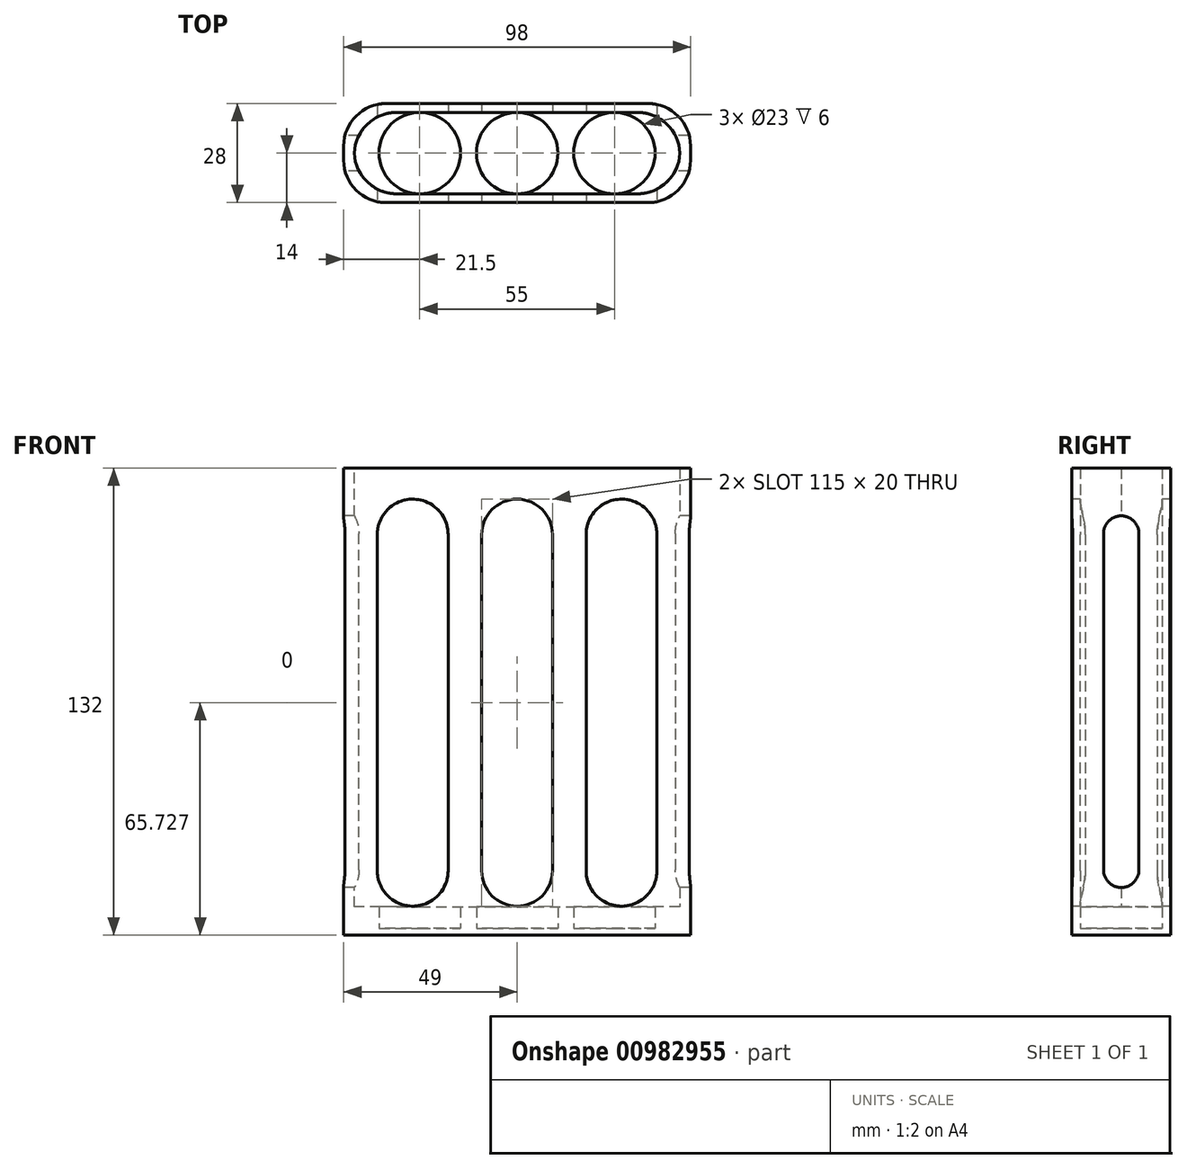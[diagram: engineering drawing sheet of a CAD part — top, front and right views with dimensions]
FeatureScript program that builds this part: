
annotation { "Feature Type Name" : "Feature", "Feature Type Description" : "" }
export const myFeature = defineFeature(function(context is Context, id is Id, definition is map)
    precondition{}
    {
        {
            var Q0;
            Q0=qCreatedBy(makeId("Top.planeOp"),FACE);
            var sketch = newSketch(context, id + "F0", { "sketchPlane" : qUnion([Q0])});
            skCircle(sketch, "E0", {"center": v(-34.5, 0) * mm, "radius": 11.5 * mm});
            skCircle(sketch, "E1.1.0.0", {"center": v(-11.5, 0) * mm, "radius": 11.5 * mm});
            skCircle(sketch, "E1.2.0.0", {"center": v(11.5, 0) * mm, "radius": 11.5 * mm});
            skCircle(sketch, "E1.3.0.0", {"center": v(34.5, 0) * mm, "radius": 11.5 * mm});
            skLineSegment(sketch, "E1.direction1", {"start": v(-34.5, 0) * mm, "end": v(-11.5, 0) * mm, "construction": true});
            skPoint(sketch, "E2", {"position": v(0, 0) * mm});
            skLineSegment(sketch, "E3.bottom", {"start": v(-34.5, 11.5) * mm, "end": v(34.5, 11.5) * mm});
            skLineSegment(sketch, "E3.top", {"start": v(-34.5, -11.5) * mm, "end": v(34.5, -11.5) * mm});
            skLineSegment(sketch, "E3.left", {"start": v(-34.5, 11.5) * mm, "end": v(-34.5, -11.5) * mm});
            skLineSegment(sketch, "E3.right", {"start": v(34.5, 11.5) * mm, "end": v(34.5, -11.5) * mm});
            skLineSegment(sketch, "E4.bottom", {"start": v(49, 14) * mm, "end": v(-49, 14) * mm});
            skLineSegment(sketch, "E4.top", {"start": v(49, -14) * mm, "end": v(-49, -14) * mm});
            skLineSegment(sketch, "E4.left", {"start": v(49, 14) * mm, "end": v(49, -14) * mm});
            skLineSegment(sketch, "E4.right", {"start": v(-49, 14) * mm, "end": v(-49, -14) * mm});
            skLineSegment(sketch, "E5.bottom", {"start": v(-34.5, 11.5) * mm, "end": v(-46, 11.5) * mm});
            skLineSegment(sketch, "E5.top", {"start": v(-34.5, 0) * mm, "end": v(-46, 0) * mm});
            skLineSegment(sketch, "E5.left", {"start": v(-34.5, 11.5) * mm, "end": v(-34.5, 0) * mm});
            skLineSegment(sketch, "E5.right", {"start": v(-46, 11.5) * mm, "end": v(-46, 0) * mm});
            skLineSegment(sketch, "E6.bottom", {"start": v(-46, 0) * mm, "end": v(-34.5, 0) * mm});
            skLineSegment(sketch, "E6.top", {"start": v(-46, -11.5) * mm, "end": v(-34.5, -11.5) * mm});
            skLineSegment(sketch, "E6.left", {"start": v(-46, 0) * mm, "end": v(-46, -11.5) * mm});
            skLineSegment(sketch, "E6.right", {"start": v(-34.5, 0) * mm, "end": v(-34.5, -11.5) * mm});
            skLineSegment(sketch, "E7.bottom", {"start": v(34.5, 11.5) * mm, "end": v(46, 11.5) * mm});
            skLineSegment(sketch, "E7.top", {"start": v(34.5, 0) * mm, "end": v(46, 0) * mm});
            skLineSegment(sketch, "E7.left", {"start": v(34.5, 11.5) * mm, "end": v(34.5, 0) * mm});
            skLineSegment(sketch, "E7.right", {"start": v(46, 11.5) * mm, "end": v(46, 0) * mm});
            skLineSegment(sketch, "E8.top", {"start": v(34.5, -11.5) * mm, "end": v(46, -11.5) * mm});
            skLineSegment(sketch, "E8.left", {"start": v(34.5, 0) * mm, "end": v(34.5, -11.5) * mm});
            skLineSegment(sketch, "E8.right", {"start": v(46, 0) * mm, "end": v(46, -11.5) * mm});
            skSolve(sketch);
        }
        {
            var Q0;
            Q0=makeQuery(id+"F0.imprint","IMPRINT",FACE,{"disambiguationData":[TD([[makeQuery(id+"F0.imprint","IMPRINT",EDGE,{"derivedFrom":sQuery(id+"F0.wireOp",EDGE,"E4.bottom")}),1.0]])]});
            var Q1;
            {var subQ0=sQuery(id+"F0.wireOp",EDGE,"E3.left");Q1=makeQuery(id+"F0.imprint","IMPRINT",FACE,{"disambiguationData":[TD([[makeQuery(id+"F0.imprint","IMPRINT",EDGE,{"derivedFrom":subQ0}),-1.0]])]});}
            var Q2;
            {var subQ0=sQuery(id+"F0.wireOp",EDGE,"E3.left");Q2=makeQuery(id+"F0.imprint","IMPRINT",FACE,{"disambiguationData":[TD([[makeQuery(id+"F0.imprint","IMPRINT",EDGE,{"derivedFrom":subQ0}),1.0]])]});}
            var Q3;
            {var subQ1=sQuery(id+"F0.wireOp",EDGE,"E0");var subQ3=sQuery(id+"F0.wireOp",EDGE,"E1.1.0.0");var subQ4=makeQuery(id+"F0.imprint","INTERSECT",VERTEX,{"derivedFrom":[subQ1,subQ3]});Q3=makeQuery(id+"F0.imprint","IMPRINT",FACE,{"disambiguationData":[TD([[makeQuery(id+"F0.imprint","IMPRINT",EDGE,{"disambiguationData":[TD([[subQ4,-1.0]])],"derivedFrom":subQ3}),-1.0]])]});}
            var Q4;
            {var subQ0=sQuery(id+"F0.wireOp",EDGE,"E1.1.0.0");var subQ1=makeQuery(id+"F0.imprint","INTERSECT",VERTEX,{"derivedFrom":[subQ0,sQuery(id+"F0.wireOp",EDGE,"E3.bottom")]});Q4=makeQuery(id+"F0.imprint","IMPRINT",FACE,{"disambiguationData":[TD([[makeQuery(id+"F0.imprint","IMPRINT",EDGE,{"disambiguationData":[TD([[subQ1,1.0]])],"derivedFrom":subQ0}),1.0]])]});}
            var Q5;
            {var subQ1=sQuery(id+"F0.wireOp",EDGE,"E0");var subQ3=sQuery(id+"F0.wireOp",EDGE,"E1.1.0.0");var subQ4=makeQuery(id+"F0.imprint","INTERSECT",VERTEX,{"derivedFrom":[subQ1,subQ3]});Q5=makeQuery(id+"F0.imprint","IMPRINT",FACE,{"disambiguationData":[TD([[makeQuery(id+"F0.imprint","IMPRINT",EDGE,{"disambiguationData":[TD([[subQ4,1.0]])],"derivedFrom":subQ3}),-1.0]])]});}
            var Q6;
            {var subQ0=sQuery(id+"F0.wireOp",EDGE,"E1.2.0.0");var subQ1=sQuery(id+"F0.wireOp",EDGE,"E1.1.0.0");var subQ2=makeQuery(id+"F0.imprint","INTERSECT",VERTEX,{"derivedFrom":[subQ1,subQ0]});Q6=makeQuery(id+"F0.imprint","IMPRINT",FACE,{"disambiguationData":[TD([[makeQuery(id+"F0.imprint","IMPRINT",EDGE,{"disambiguationData":[TD([[subQ2,1.0]])],"derivedFrom":subQ1}),-1.0]])]});}
            var Q7;
            {var subQ0=sQuery(id+"F0.wireOp",EDGE,"E3.bottom");var subQ1=sQuery(id+"F0.wireOp",EDGE,"E1.1.0.0");var subQ2=makeQuery(id+"F0.imprint","INTERSECT",VERTEX,{"derivedFrom":[subQ1,subQ0]});Q7=makeQuery(id+"F0.imprint","IMPRINT",FACE,{"disambiguationData":[TD([[makeQuery(id+"F0.imprint","IMPRINT",EDGE,{"disambiguationData":[TD([[subQ2,1.0]])],"derivedFrom":subQ1}),-1.0]])]});}
            var Q8;
            {var subQ0=sQuery(id+"F0.wireOp",EDGE,"E1.2.0.0");var subQ1=makeQuery(id+"F0.imprint","INTERSECT",VERTEX,{"derivedFrom":[subQ0,sQuery(id+"F0.wireOp",EDGE,"E3.bottom")]});Q8=makeQuery(id+"F0.imprint","IMPRINT",FACE,{"disambiguationData":[TD([[makeQuery(id+"F0.imprint","IMPRINT",EDGE,{"disambiguationData":[TD([[subQ1,1.0]])],"derivedFrom":subQ0}),1.0]])]});}
            var Q9;
            {var subQ0=sQuery(id+"F0.wireOp",EDGE,"E3.right");Q9=makeQuery(id+"F0.imprint","IMPRINT",FACE,{"disambiguationData":[TD([[makeQuery(id+"F0.imprint","IMPRINT",EDGE,{"derivedFrom":subQ0}),-1.0]])]});}
            var Q10;
            {var subQ0=sQuery(id+"F0.wireOp",EDGE,"E3.right");Q10=makeQuery(id+"F0.imprint","IMPRINT",FACE,{"disambiguationData":[TD([[makeQuery(id+"F0.imprint","IMPRINT",EDGE,{"derivedFrom":subQ0}),1.0]])]});}
            var Q11;
            {var subQ0=sQuery(id+"F0.wireOp",EDGE,"E1.3.0.0");var subQ1=sQuery(id+"F0.wireOp",EDGE,"E1.2.0.0");var subQ2=makeQuery(id+"F0.imprint","INTERSECT",VERTEX,{"derivedFrom":[subQ1,subQ0]});Q11=makeQuery(id+"F0.imprint","IMPRINT",FACE,{"disambiguationData":[TD([[makeQuery(id+"F0.imprint","IMPRINT",EDGE,{"disambiguationData":[TD([[subQ2,1.0]])],"derivedFrom":subQ1}),-1.0]])]});}
            var Q12;
            {var subQ0=sQuery(id+"F0.wireOp",EDGE,"E3.bottom");var subQ1=sQuery(id+"F0.wireOp",EDGE,"E1.2.0.0");var subQ2=makeQuery(id+"F0.imprint","INTERSECT",VERTEX,{"derivedFrom":[subQ1,subQ0]});Q12=makeQuery(id+"F0.imprint","IMPRINT",FACE,{"disambiguationData":[TD([[makeQuery(id+"F0.imprint","IMPRINT",EDGE,{"disambiguationData":[TD([[subQ2,1.0]])],"derivedFrom":subQ1}),-1.0]])]});}
            var Q13;
            {var subQ0=sQuery(id+"F0.wireOp",EDGE,"E5.left");Q13=makeQuery(id+"F0.imprint","IMPRINT",FACE,{"disambiguationData":[TD([[makeQuery(id+"F0.imprint","IMPRINT",EDGE,{"derivedFrom":subQ0}),-1.0]])]});}
            var Q14;
            {var subQ2=sQuery(id+"F0.wireOp",EDGE,"E6.bottom");Q14=makeQuery(id+"F0.imprint","IMPRINT",FACE,{"disambiguationData":[TD([[makeQuery(id+"F0.imprint","IMPRINT",EDGE,{"derivedFrom":subQ2}),-1.0]])]});}
            var Q15;
            {var subQ0=sQuery(id+"F0.wireOp",EDGE,"E6.top");Q15=makeQuery(id+"F0.imprint","IMPRINT",FACE,{"disambiguationData":[TD([[makeQuery(id+"F0.imprint","IMPRINT",EDGE,{"derivedFrom":subQ0}),1.0]])]});}
            var Q16;
            {var subQ0=sQuery(id+"F0.wireOp",EDGE,"E5.left");Q16=makeQuery(id+"F0.imprint","IMPRINT",FACE,{"disambiguationData":[TD([[makeQuery(id+"F0.imprint","IMPRINT",EDGE,{"derivedFrom":subQ0}),1.0]])]});}
            var Q17;
            {var subQ0=sQuery(id+"F0.wireOp",EDGE,"E5.bottom");Q17=makeQuery(id+"F0.imprint","IMPRINT",FACE,{"disambiguationData":[TD([[makeQuery(id+"F0.imprint","IMPRINT",EDGE,{"derivedFrom":subQ0}),1.0]])]});}
            var Q18;
            {var subQ0=sQuery(id+"F0.wireOp",EDGE,"E7.left");Q18=makeQuery(id+"F0.imprint","IMPRINT",FACE,{"disambiguationData":[TD([[makeQuery(id+"F0.imprint","IMPRINT",EDGE,{"derivedFrom":subQ0}),-1.0]])]});}
            var Q19;
            {var subQ0=sQuery(id+"F0.wireOp",EDGE,"E7.left");Q19=makeQuery(id+"F0.imprint","IMPRINT",FACE,{"disambiguationData":[TD([[makeQuery(id+"F0.imprint","IMPRINT",EDGE,{"derivedFrom":subQ0}),1.0]])]});}
            var Q20;
            {var subQ0=sQuery(id+"F0.wireOp",EDGE,"E7.bottom");Q20=makeQuery(id+"F0.imprint","IMPRINT",FACE,{"disambiguationData":[TD([[makeQuery(id+"F0.imprint","IMPRINT",EDGE,{"derivedFrom":subQ0}),-1.0]])]});}
            var Q21;
            {var subQ2=sQuery(id+"F0.wireOp",EDGE,"E7.top");Q21=makeQuery(id+"F0.imprint","IMPRINT",FACE,{"disambiguationData":[TD([[makeQuery(id+"F0.imprint","IMPRINT",EDGE,{"derivedFrom":subQ2}),-1.0]])]});}
            var Q22;
            {var subQ0=sQuery(id+"F0.wireOp",EDGE,"E8.top");Q22=makeQuery(id+"F0.imprint","IMPRINT",FACE,{"disambiguationData":[TD([[makeQuery(id+"F0.imprint","IMPRINT",EDGE,{"derivedFrom":subQ0}),1.0]])]});}
            extrude(context, id + "F1", {"entities" : qUnion([Q0, Q1, Q2, Q3, Q4, Q5, Q6, Q7, Q8, Q9, Q10, Q11, Q12, Q13, Q14, Q15, Q16, Q17, Q18, Q19, Q20, Q21, Q22]), "oppositeDirection" : true, "depth" : 2 * mm, "offsetDistance" : 25 * mm});
        }
        {
            var Q0;
            Q0=makeQuery(id+"F0.imprint","IMPRINT",FACE,{"disambiguationData":[TD([[makeQuery(id+"F0.imprint","IMPRINT",EDGE,{"derivedFrom":sQuery(id+"F0.wireOp",EDGE,"E4.bottom")}),1.0]])]});
            extrude(context, id + "F2", {"entities" : qUnion([Q0]), "operationType" : NewBodyOperationType.ADD, "depth" : 130 * mm, "offsetDistance" : 25 * mm});
        }
        {
            var Q0;
            {var subQ0=sQuery(id+"F0.wireOp",EDGE,"E4.right");var subQ1=sQuery(id+"F0.wireOp",EDGE,"E4.bottom");Q0=makeQuery(id+"F2.boolean.opBoolean","MERGE",EDGE,{"derivedFrom":[makeQuery(id+"F1.opExtrude","SWEPT_EDGE",EDGE,{"disambiguationData":[OSD([subQ1,subQ0])]}),makeQuery(id+"F2.opExtrude","SWEPT_EDGE",EDGE,{"disambiguationData":[OSD([subQ1,subQ0])]})]});}
            var Q1;
            {var subQ0=sQuery(id+"F0.wireOp",EDGE,"E4.right");var subQ1=sQuery(id+"F0.wireOp",EDGE,"E4.top");Q1=makeQuery(id+"F2.boolean.opBoolean","MERGE",EDGE,{"derivedFrom":[makeQuery(id+"F1.opExtrude","SWEPT_EDGE",EDGE,{"disambiguationData":[OSD([subQ1,subQ0])]}),makeQuery(id+"F2.opExtrude","SWEPT_EDGE",EDGE,{"disambiguationData":[OSD([subQ1,subQ0])]})]});}
            var Q2;
            {var subQ0=sQuery(id+"F0.wireOp",EDGE,"E4.left");var subQ1=sQuery(id+"F0.wireOp",EDGE,"E4.top");Q2=makeQuery(id+"F2.boolean.opBoolean","MERGE",EDGE,{"derivedFrom":[makeQuery(id+"F1.opExtrude","SWEPT_EDGE",EDGE,{"disambiguationData":[OSD([subQ1,subQ0])]}),makeQuery(id+"F2.opExtrude","SWEPT_EDGE",EDGE,{"disambiguationData":[OSD([subQ1,subQ0])]})]});}
            var Q3;
            {var subQ0=sQuery(id+"F0.wireOp",EDGE,"E4.left");var subQ1=sQuery(id+"F0.wireOp",EDGE,"E4.bottom");Q3=makeQuery(id+"F2.boolean.opBoolean","MERGE",EDGE,{"derivedFrom":[makeQuery(id+"F1.opExtrude","SWEPT_EDGE",EDGE,{"disambiguationData":[OSD([subQ1,subQ0])]}),makeQuery(id+"F2.opExtrude","SWEPT_EDGE",EDGE,{"disambiguationData":[OSD([subQ1,subQ0])]})]});}
            var Q4;
            Q4=makeQuery(id+"F2.opExtrude","SWEPT_EDGE",EDGE,{"disambiguationData":[OSD([sQuery(id+"F0.wireOp",EDGE,"E7.bottom"),sQuery(id+"F0.wireOp",EDGE,"E7.right")])]});
            var Q5;
            Q5=makeQuery(id+"F2.opExtrude","SWEPT_EDGE",EDGE,{"disambiguationData":[OSD([sQuery(id+"F0.wireOp",EDGE,"E8.top"),sQuery(id+"F0.wireOp",EDGE,"E8.right")])]});
            var Q6;
            Q6=makeQuery(id+"F2.opExtrude","SWEPT_EDGE",EDGE,{"disambiguationData":[OSD([sQuery(id+"F0.wireOp",EDGE,"E5.bottom"),sQuery(id+"F0.wireOp",EDGE,"E5.right")])]});
            var Q7;
            Q7=makeQuery(id+"F2.opExtrude","SWEPT_EDGE",EDGE,{"disambiguationData":[OSD([sQuery(id+"F0.wireOp",EDGE,"E6.top"),sQuery(id+"F0.wireOp",EDGE,"E6.left")])]});
            fillet(context, id + "F3", {"entities" : qUnion([Q0, Q1, Q2, Q3, Q4, Q5, Q6, Q7]), "radius" : 12 * mm, "tangentPropagation" : true, "allowEdgeOverflow" : false});
        }
        {
            var Q0;
            {var subQ0=sQuery(id+"F0.wireOp",EDGE,"E4.top");Q0=makeQuery(id+"F2.boolean.opBoolean","MERGE",FACE,{"derivedFrom":[makeQuery(id+"F1.opExtrude","SWEPT_FACE",FACE,{"disambiguationData":[OSD([subQ0])]}),makeQuery(id+"F2.opExtrude","SWEPT_FACE",FACE,{"disambiguationData":[OSD([subQ0])]})]});}
            var sketch = newSketch(context, id + "F4", { "sketchPlane" : qUnion([Q0])});
            skLineSegment(sketch, "E9.bottom", {"start": v(-10, 111.23) * mm, "end": v(10, 111.23) * mm});
            skLineSegment(sketch, "E9.top", {"start": v(-10, 16.23) * mm, "end": v(10, 16.23) * mm});
            skLineSegment(sketch, "E9.left", {"start": v(-10, 111.23) * mm, "end": v(-10, 16.23) * mm});
            skLineSegment(sketch, "E9.right", {"start": v(10, 111.23) * mm, "end": v(10, 16.23) * mm});
            skPoint(sketch, "E9.middle", {"position": v(0, 63.73) * mm});
            skArc(sketch, "E10", {"start": v(10, 111.23) * mm, "mid": v(0, 121.23) * mm, "end": v(-10, 111.23) * mm});
            skArc(sketch, "E11", {"start": v(-10, 16.23) * mm, "mid": v(0, 6.23) * mm, "end": v(10, 16.23) * mm});
            skLineSegment(sketch, "E12.bottom", {"start": v(-19.5, 111.23) * mm, "end": v(-39.5, 111.23) * mm});
            skLineSegment(sketch, "E12.top", {"start": v(-19.5, 16.23) * mm, "end": v(-39.5, 16.23) * mm});
            skLineSegment(sketch, "E12.left", {"start": v(-19.5, 111.23) * mm, "end": v(-19.5, 16.23) * mm});
            skLineSegment(sketch, "E12.right", {"start": v(-39.5, 111.23) * mm, "end": v(-39.5, 16.23) * mm});
            skPoint(sketch, "E12.middle", {"position": v(-29.5, 63.73) * mm});
            skArc(sketch, "E13", {"start": v(-19.5, 111.23) * mm, "mid": v(-29.5, 121.23) * mm, "end": v(-39.5, 111.23) * mm});
            skArc(sketch, "E14", {"start": v(-39.5, 16.23) * mm, "mid": v(-29.5, 6.23) * mm, "end": v(-19.5, 16.23) * mm});
            skLineSegment(sketch, "E15.bottom", {"start": v(39.5, 111.23) * mm, "end": v(19.5, 111.23) * mm});
            skLineSegment(sketch, "E15.top", {"start": v(39.5, 16.23) * mm, "end": v(19.5, 16.23) * mm});
            skLineSegment(sketch, "E15.left", {"start": v(39.5, 111.23) * mm, "end": v(39.5, 16.23) * mm});
            skLineSegment(sketch, "E15.right", {"start": v(19.5, 111.23) * mm, "end": v(19.5, 16.23) * mm});
            skPoint(sketch, "E15.middle", {"position": v(29.5, 63.73) * mm});
            skArc(sketch, "E16", {"start": v(39.5, 111.23) * mm, "mid": v(29.5, 121.23) * mm, "end": v(19.5, 111.23) * mm});
            skArc(sketch, "E17", {"start": v(19.5, 16.23) * mm, "mid": v(29.5, 6.23) * mm, "end": v(39.5, 16.23) * mm});
            skLineSegment(sketch, "E18", {"start": v(0, 130) * mm, "end": v(0, -2) * mm, "construction": true});
            skSolve(sketch);
        }
        {
            var Q0;
            {var subQ0=sQuery(id+"F4.wireOp",EDGE,"E12.left");Q0=makeQuery(id+"F4.imprint","IMPRINT",FACE,{"disambiguationData":[TD([[makeQuery(id+"F4.imprint","IMPRINT",EDGE,{"derivedFrom":subQ0}),-1.0]])]});}
            var Q1;
            {var subQ0=sQuery(id+"F4.wireOp",EDGE,"E12.right");Q1=makeQuery(id+"F4.imprint","IMPRINT",FACE,{"disambiguationData":[TD([[makeQuery(id+"F4.imprint","IMPRINT",EDGE,{"derivedFrom":subQ0}),1.0]])]});}
            var Q2;
            {var subQ0=sQuery(id+"F4.wireOp",EDGE,"E13");var subQ1=sQuery(id+"F4.wireOp",EDGE,"E12.bottom");var subQ2=makeQuery(id+"F4.imprint","INTERSECT",VERTEX,{"derivedFrom":[subQ1,sQuery(id+"F4.wireOp",EDGE,"E12.left"),subQ0]});Q2=makeQuery(id+"F4.imprint","IMPRINT",FACE,{"disambiguationData":[TD([[makeQuery(id+"F4.imprint","IMPRINT",EDGE,{"disambiguationData":[TD([[subQ2,-1.0]])],"derivedFrom":subQ1}),-1.0]])]});}
            var Q3;
            {var subQ0=sQuery(id+"F4.wireOp",EDGE,"E13");var subQ1=sQuery(id+"F4.wireOp",EDGE,"E12.bottom");var subQ2=makeQuery(id+"F4.imprint","INTERSECT",VERTEX,{"derivedFrom":[subQ1,sQuery(id+"F4.wireOp",EDGE,"E12.right"),subQ0]});Q3=makeQuery(id+"F4.imprint","IMPRINT",FACE,{"disambiguationData":[TD([[makeQuery(id+"F4.imprint","IMPRINT",EDGE,{"disambiguationData":[TD([[subQ2,1.0]])],"derivedFrom":subQ1}),-1.0]])]});}
            var Q4;
            Q4=makeQuery(id+"F4.imprint","IMPRINT",FACE,{"disambiguationData":[TD([[makeQuery(id+"F4.imprint","IMPRINT",EDGE,{"derivedFrom":sQuery(id+"F4.wireOp",EDGE,"E9.bottom")}),1.0]])]});
            var Q5;
            Q5=makeQuery(id+"F4.imprint","IMPRINT",FACE,{"disambiguationData":[TD([[makeQuery(id+"F4.imprint","IMPRINT",EDGE,{"derivedFrom":sQuery(id+"F4.wireOp",EDGE,"E9.bottom")}),-1.0]])]});
            var Q6;
            {var subQ0=sQuery(id+"F4.wireOp",EDGE,"E14");var subQ1=sQuery(id+"F4.wireOp",EDGE,"E12.top");var subQ2=makeQuery(id+"F4.imprint","INTERSECT",VERTEX,{"derivedFrom":[subQ1,sQuery(id+"F4.wireOp",EDGE,"E12.left"),subQ0]});Q6=makeQuery(id+"F4.imprint","IMPRINT",FACE,{"disambiguationData":[TD([[makeQuery(id+"F4.imprint","IMPRINT",EDGE,{"disambiguationData":[TD([[subQ2,-1.0]])],"derivedFrom":subQ1}),1.0]])]});}
            var Q7;
            {var subQ0=sQuery(id+"F4.wireOp",EDGE,"E14");var subQ1=sQuery(id+"F4.wireOp",EDGE,"E12.top");var subQ2=makeQuery(id+"F4.imprint","INTERSECT",VERTEX,{"derivedFrom":[subQ1,sQuery(id+"F4.wireOp",EDGE,"E12.right"),subQ0]});Q7=makeQuery(id+"F4.imprint","IMPRINT",FACE,{"disambiguationData":[TD([[makeQuery(id+"F4.imprint","IMPRINT",EDGE,{"disambiguationData":[TD([[subQ2,1.0]])],"derivedFrom":subQ1}),1.0]])]});}
            var Q8;
            Q8=makeQuery(id+"F4.imprint","IMPRINT",FACE,{"disambiguationData":[TD([[makeQuery(id+"F4.imprint","IMPRINT",EDGE,{"derivedFrom":sQuery(id+"F4.wireOp",EDGE,"E9.top")}),-1.0]])]});
            var Q9;
            {var subQ0=sQuery(id+"F4.wireOp",EDGE,"E17");var subQ1=sQuery(id+"F4.wireOp",EDGE,"E15.top");var subQ2=makeQuery(id+"F4.imprint","INTERSECT",VERTEX,{"derivedFrom":[subQ1,sQuery(id+"F4.wireOp",EDGE,"E15.right"),subQ0]});Q9=makeQuery(id+"F4.imprint","IMPRINT",FACE,{"disambiguationData":[TD([[makeQuery(id+"F4.imprint","IMPRINT",EDGE,{"disambiguationData":[TD([[subQ2,1.0]])],"derivedFrom":subQ1}),1.0]])]});}
            var Q10;
            {var subQ0=sQuery(id+"F4.wireOp",EDGE,"E17");var subQ1=sQuery(id+"F4.wireOp",EDGE,"E15.top");var subQ2=makeQuery(id+"F4.imprint","INTERSECT",VERTEX,{"derivedFrom":[subQ1,sQuery(id+"F4.wireOp",EDGE,"E15.left"),subQ0]});Q10=makeQuery(id+"F4.imprint","IMPRINT",FACE,{"disambiguationData":[TD([[makeQuery(id+"F4.imprint","IMPRINT",EDGE,{"disambiguationData":[TD([[subQ2,-1.0]])],"derivedFrom":subQ1}),1.0]])]});}
            var Q11;
            {var subQ0=sQuery(id+"F4.wireOp",EDGE,"E15.left");Q11=makeQuery(id+"F4.imprint","IMPRINT",FACE,{"disambiguationData":[TD([[makeQuery(id+"F4.imprint","IMPRINT",EDGE,{"derivedFrom":subQ0}),-1.0]])]});}
            var Q12;
            {var subQ0=sQuery(id+"F4.wireOp",EDGE,"E15.right");Q12=makeQuery(id+"F4.imprint","IMPRINT",FACE,{"disambiguationData":[TD([[makeQuery(id+"F4.imprint","IMPRINT",EDGE,{"derivedFrom":subQ0}),1.0]])]});}
            var Q13;
            {var subQ0=sQuery(id+"F4.wireOp",EDGE,"E16");var subQ1=sQuery(id+"F4.wireOp",EDGE,"E15.bottom");var subQ2=makeQuery(id+"F4.imprint","INTERSECT",VERTEX,{"derivedFrom":[subQ1,sQuery(id+"F4.wireOp",EDGE,"E15.right"),subQ0]});Q13=makeQuery(id+"F4.imprint","IMPRINT",FACE,{"disambiguationData":[TD([[makeQuery(id+"F4.imprint","IMPRINT",EDGE,{"disambiguationData":[TD([[subQ2,1.0]])],"derivedFrom":subQ1}),-1.0]])]});}
            var Q14;
            {var subQ0=sQuery(id+"F4.wireOp",EDGE,"E16");var subQ1=sQuery(id+"F4.wireOp",EDGE,"E15.bottom");var subQ2=makeQuery(id+"F4.imprint","INTERSECT",VERTEX,{"derivedFrom":[subQ1,sQuery(id+"F4.wireOp",EDGE,"E15.left"),subQ0]});Q14=makeQuery(id+"F4.imprint","IMPRINT",FACE,{"disambiguationData":[TD([[makeQuery(id+"F4.imprint","IMPRINT",EDGE,{"disambiguationData":[TD([[subQ2,-1.0]])],"derivedFrom":subQ1}),-1.0]])]});}
            extrude(context, id + "F5", {"entities" : qUnion([Q0, Q1, Q2, Q3, Q4, Q5, Q6, Q7, Q8, Q9, Q10, Q11, Q12, Q13, Q14]), "operationType" : NewBodyOperationType.REMOVE, "oppositeDirection" : true, "depth" : 50 * mm, "offsetDistance" : 25 * mm});
        }
        {
            var Q0;
            {var subQ0=sQuery(id+"F0.wireOp",EDGE,"E4.right");Q0=makeQuery(id+"F2.boolean.opBoolean","MERGE",FACE,{"derivedFrom":[makeQuery(id+"F1.opExtrude","SWEPT_FACE",FACE,{"disambiguationData":[OSD([subQ0])]}),makeQuery(id+"F2.opExtrude","SWEPT_FACE",FACE,{"disambiguationData":[OSD([subQ0])]})]});}
            var sketch = newSketch(context, id + "F6", { "sketchPlane" : qUnion([Q0])});
            skLineSegment(sketch, "E19", {"start": v(2, 64) * mm, "end": v(-2, 64) * mm, "construction": true});
            skPoint(sketch, "E20", {"position": v(0, 64) * mm});
            skLineSegment(sketch, "E21.bottom", {"start": v(5, 111.5) * mm, "end": v(-5, 111.5) * mm});
            skLineSegment(sketch, "E21.top", {"start": v(5, 16.5) * mm, "end": v(-5, 16.5) * mm});
            skLineSegment(sketch, "E21.left", {"start": v(5, 111.5) * mm, "end": v(5, 16.5) * mm});
            skLineSegment(sketch, "E21.right", {"start": v(-5, 111.5) * mm, "end": v(-5, 16.5) * mm});
            skArc(sketch, "E22", {"start": v(5, 111.5) * mm, "mid": v(0, 116.5) * mm, "end": v(-5, 111.5) * mm});
            skArc(sketch, "E23", {"start": v(-5, 16.5) * mm, "mid": v(0, 11.5) * mm, "end": v(5, 16.5) * mm});
            skSolve(sketch);
        }
        {
            var Q0;
            {var subQ0=sQuery(id+"F6.wireOp",EDGE,"E22");var subQ1=sQuery(id+"F6.wireOp",EDGE,"E21.bottom");var subQ2=makeQuery(id+"F6.imprint","INTERSECT",VERTEX,{"derivedFrom":[subQ1,sQuery(id+"F6.wireOp",EDGE,"E21.right"),subQ0]});Q0=makeQuery(id+"F6.imprint","IMPRINT",FACE,{"disambiguationData":[TD([[makeQuery(id+"F6.imprint","IMPRINT",EDGE,{"disambiguationData":[TD([[subQ2,1.0]])],"derivedFrom":subQ1}),-1.0]])]});}
            var Q1;
            {var subQ0=sQuery(id+"F6.wireOp",EDGE,"E21.bottom");var subQ1=sQuery(id+"F0.wireOp",EDGE,"E4.right");var subQ2=makeQuery(id+"F2.boolean.opBoolean","MERGE",FACE,{"derivedFrom":[makeQuery(id+"F1.opExtrude","SWEPT_FACE",FACE,{"disambiguationData":[OSD([subQ1])]}),makeQuery(id+"F2.opExtrude","SWEPT_FACE",FACE,{"disambiguationData":[OSD([subQ1])]})]});var subQ3=sQuery(id+"F0.wireOp",EDGE,"E4.top");var subQ4=makeQuery(id+"F3.opFillet","BLEND_EDGE",EDGE,{"blendedFrom":[makeQuery(id+"F2.boolean.opBoolean","MERGE",EDGE,{"derivedFrom":[makeQuery(id+"F1.opExtrude","SWEPT_EDGE",EDGE,{"disambiguationData":[OSD([subQ3,subQ1])]}),makeQuery(id+"F2.opExtrude","SWEPT_EDGE",EDGE,{"disambiguationData":[OSD([subQ3,subQ1])]})]}),subQ2],"blendedInto":[subQ2]});var subQ5=makeQuery(id+"F6.imprint","INTERSECT",VERTEX,{"derivedFrom":[subQ4,subQ0]});Q1=makeQuery(id+"F6.imprint","IMPRINT",FACE,{"disambiguationData":[TD([[makeQuery(id+"F6.imprint","IMPRINT",EDGE,{"disambiguationData":[TD([[subQ5,-1.0]])],"derivedFrom":subQ0}),-1.0]])]});}
            var Q2;
            {var subQ0=sQuery(id+"F6.wireOp",EDGE,"E21.left");Q2=makeQuery(id+"F6.imprint","IMPRINT",FACE,{"disambiguationData":[TD([[makeQuery(id+"F6.imprint","IMPRINT",EDGE,{"derivedFrom":subQ0}),-1.0]])]});}
            var Q3;
            {var subQ0=sQuery(id+"F6.wireOp",EDGE,"E21.bottom");var subQ1=sQuery(id+"F0.wireOp",EDGE,"E4.right");var subQ2=makeQuery(id+"F2.boolean.opBoolean","MERGE",FACE,{"derivedFrom":[makeQuery(id+"F1.opExtrude","SWEPT_FACE",FACE,{"disambiguationData":[OSD([subQ1])]}),makeQuery(id+"F2.opExtrude","SWEPT_FACE",FACE,{"disambiguationData":[OSD([subQ1])]})]});var subQ3=sQuery(id+"F0.wireOp",EDGE,"E4.top");var subQ4=makeQuery(id+"F3.opFillet","BLEND_EDGE",EDGE,{"blendedFrom":[makeQuery(id+"F2.boolean.opBoolean","MERGE",EDGE,{"derivedFrom":[makeQuery(id+"F1.opExtrude","SWEPT_EDGE",EDGE,{"disambiguationData":[OSD([subQ3,subQ1])]}),makeQuery(id+"F2.opExtrude","SWEPT_EDGE",EDGE,{"disambiguationData":[OSD([subQ3,subQ1])]})]}),subQ2],"blendedInto":[subQ2]});var subQ5=makeQuery(id+"F6.imprint","INTERSECT",VERTEX,{"derivedFrom":[subQ4,subQ0]});Q3=makeQuery(id+"F6.imprint","IMPRINT",FACE,{"disambiguationData":[TD([[makeQuery(id+"F6.imprint","IMPRINT",EDGE,{"disambiguationData":[TD([[subQ5,-1.0]])],"derivedFrom":subQ0}),1.0]])]});}
            var Q4;
            {var subQ0=sQuery(id+"F6.wireOp",EDGE,"E21.right");Q4=makeQuery(id+"F6.imprint","IMPRINT",FACE,{"disambiguationData":[TD([[makeQuery(id+"F6.imprint","IMPRINT",EDGE,{"derivedFrom":subQ0}),1.0]])]});}
            var Q5;
            {var subQ0=sQuery(id+"F6.wireOp",EDGE,"E23");var subQ1=sQuery(id+"F6.wireOp",EDGE,"E21.top");var subQ2=makeQuery(id+"F6.imprint","INTERSECT",VERTEX,{"derivedFrom":[subQ1,sQuery(id+"F6.wireOp",EDGE,"E21.right"),subQ0]});Q5=makeQuery(id+"F6.imprint","IMPRINT",FACE,{"disambiguationData":[TD([[makeQuery(id+"F6.imprint","IMPRINT",EDGE,{"disambiguationData":[TD([[subQ2,1.0]])],"derivedFrom":subQ1}),1.0]])]});}
            var Q6;
            {var subQ0=sQuery(id+"F6.wireOp",EDGE,"E21.top");var subQ1=sQuery(id+"F0.wireOp",EDGE,"E4.right");var subQ2=makeQuery(id+"F2.boolean.opBoolean","MERGE",FACE,{"derivedFrom":[makeQuery(id+"F1.opExtrude","SWEPT_FACE",FACE,{"disambiguationData":[OSD([subQ1])]}),makeQuery(id+"F2.opExtrude","SWEPT_FACE",FACE,{"disambiguationData":[OSD([subQ1])]})]});var subQ3=sQuery(id+"F0.wireOp",EDGE,"E4.top");var subQ4=makeQuery(id+"F3.opFillet","BLEND_EDGE",EDGE,{"blendedFrom":[makeQuery(id+"F2.boolean.opBoolean","MERGE",EDGE,{"derivedFrom":[makeQuery(id+"F1.opExtrude","SWEPT_EDGE",EDGE,{"disambiguationData":[OSD([subQ3,subQ1])]}),makeQuery(id+"F2.opExtrude","SWEPT_EDGE",EDGE,{"disambiguationData":[OSD([subQ3,subQ1])]})]}),subQ2],"blendedInto":[subQ2]});var subQ5=makeQuery(id+"F6.imprint","INTERSECT",VERTEX,{"derivedFrom":[subQ4,subQ0]});Q6=makeQuery(id+"F6.imprint","IMPRINT",FACE,{"disambiguationData":[TD([[makeQuery(id+"F6.imprint","IMPRINT",EDGE,{"disambiguationData":[TD([[subQ5,-1.0]])],"derivedFrom":subQ0}),1.0]])]});}
            var Q7;
            {var subQ0=sQuery(id+"F6.wireOp",EDGE,"E23");var subQ1=sQuery(id+"F6.wireOp",EDGE,"E21.top");var subQ2=makeQuery(id+"F6.imprint","INTERSECT",VERTEX,{"derivedFrom":[subQ1,sQuery(id+"F6.wireOp",EDGE,"E21.left"),subQ0]});Q7=makeQuery(id+"F6.imprint","IMPRINT",FACE,{"disambiguationData":[TD([[makeQuery(id+"F6.imprint","IMPRINT",EDGE,{"disambiguationData":[TD([[subQ2,-1.0]])],"derivedFrom":subQ1}),1.0]])]});}
            var Q8;
            {var subQ0=sQuery(id+"F6.wireOp",EDGE,"E22");var subQ1=sQuery(id+"F6.wireOp",EDGE,"E21.bottom");var subQ2=makeQuery(id+"F6.imprint","INTERSECT",VERTEX,{"derivedFrom":[subQ1,sQuery(id+"F6.wireOp",EDGE,"E21.left"),subQ0]});Q8=makeQuery(id+"F6.imprint","IMPRINT",FACE,{"disambiguationData":[TD([[makeQuery(id+"F6.imprint","IMPRINT",EDGE,{"disambiguationData":[TD([[subQ2,-1.0]])],"derivedFrom":subQ1}),-1.0]])]});}
            extrude(context, id + "F7", {"entities" : qUnion([Q0, Q1, Q2, Q3, Q4, Q5, Q6, Q7, Q8]), "operationType" : NewBodyOperationType.REMOVE, "oppositeDirection" : true, "depth" : 100 * mm, "offsetDistance" : 25 * mm});
        }
        {
            var Q0;
            Q0=makeQuery(id+"F1.opExtrude","CAP_FACE",FACE,{"disambiguationData":[OSD([sQuery(id+"F0.wireOp",EDGE,"E4.bottom"),sQuery(id+"F0.wireOp",EDGE,"E4.top"),sQuery(id+"F0.wireOp",EDGE,"E4.left"),sQuery(id+"F0.wireOp",EDGE,"E4.right")])],"isStart":true});
            var sketch = newSketch(context, id + "F8", { "sketchPlane" : qUnion([Q0])});
            skCircle(sketch, "E24", {"center": v(-27.5, 0) * mm, "radius": 11.5 * mm});
            skCircle(sketch, "E25", {"center": v(0, 0) * mm, "radius": 11.5 * mm});
            skCircle(sketch, "E26", {"center": v(27.5, 0) * mm, "radius": 11.5 * mm});
            skSolve(sketch);
        }
        {
            var Q0;
            {var subQ0=sQuery(id+"F8.wireOp",EDGE,"E24");var subQ1=makeQuery(id+"F2.opExtrude","CAP_EDGE",EDGE,{"disambiguationData":[OSD([sQuery(id+"F0.wireOp",EDGE,"E3.bottom"),sQuery(id+"F0.wireOp",EDGE,"E5.bottom"),sQuery(id+"F0.wireOp",EDGE,"E7.bottom")])],"isStart":true});var subQ2=makeQuery(id+"F8.imprint","INTERSECT",VERTEX,{"derivedFrom":[subQ1,subQ0]});Q0=makeQuery(id+"F8.imprint","IMPRINT",FACE,{"disambiguationData":[TD([[makeQuery(id+"F8.imprint","IMPRINT",EDGE,{"disambiguationData":[TD([[subQ2,1.0]])],"derivedFrom":subQ0}),-1.0]])]});}
            var Q1;
            {var subQ0=makeQuery(id+"F1.opExtrude","CAP_FACE",FACE,{"disambiguationData":[OSD([sQuery(id+"F0.wireOp",EDGE,"E4.bottom"),sQuery(id+"F0.wireOp",EDGE,"E4.top"),sQuery(id+"F0.wireOp",EDGE,"E4.left"),sQuery(id+"F0.wireOp",EDGE,"E4.right")])],"isStart":true});var subQ3=sQuery(id+"F0.wireOp",EDGE,"E5.bottom");var subQ4=makeQuery(id+"F3.opFillet","BLEND_EDGE",EDGE,{"blendedFrom":[makeQuery(id+"F2.opExtrude","SWEPT_EDGE",EDGE,{"disambiguationData":[OSD([subQ3,sQuery(id+"F0.wireOp",EDGE,"E5.right")])]}),subQ0],"blendedInto":[subQ0]});Q1=makeQuery(id+"F8.imprint","IMPRINT",FACE,{"disambiguationData":[TD([[makeQuery(id+"F8.imprint","IMPRINT",EDGE,{"derivedFrom":subQ4}),1.0]])]});}
            var Q2;
            {var subQ0=sQuery(id+"F8.wireOp",EDGE,"E25");var subQ1=makeQuery(id+"F2.opExtrude","CAP_EDGE",EDGE,{"disambiguationData":[OSD([sQuery(id+"F0.wireOp",EDGE,"E3.bottom"),sQuery(id+"F0.wireOp",EDGE,"E5.bottom"),sQuery(id+"F0.wireOp",EDGE,"E7.bottom")])],"isStart":true});var subQ2=makeQuery(id+"F8.imprint","INTERSECT",VERTEX,{"derivedFrom":[subQ1,subQ0]});Q2=makeQuery(id+"F8.imprint","IMPRINT",FACE,{"disambiguationData":[TD([[makeQuery(id+"F8.imprint","IMPRINT",EDGE,{"disambiguationData":[TD([[subQ2,1.0]])],"derivedFrom":subQ0}),-1.0]])]});}
            var Q3;
            {var subQ0=sQuery(id+"F0.wireOp",EDGE,"E7.bottom");var subQ2=makeQuery(id+"F1.opExtrude","CAP_FACE",FACE,{"disambiguationData":[OSD([sQuery(id+"F0.wireOp",EDGE,"E4.bottom"),sQuery(id+"F0.wireOp",EDGE,"E4.top"),sQuery(id+"F0.wireOp",EDGE,"E4.left"),sQuery(id+"F0.wireOp",EDGE,"E4.right")])],"isStart":true});var subQ3=makeQuery(id+"F3.opFillet","BLEND_EDGE",EDGE,{"blendedFrom":[makeQuery(id+"F2.opExtrude","SWEPT_EDGE",EDGE,{"disambiguationData":[OSD([subQ0,sQuery(id+"F0.wireOp",EDGE,"E7.right")])]}),subQ2],"blendedInto":[subQ2]});Q3=makeQuery(id+"F8.imprint","IMPRINT",FACE,{"disambiguationData":[TD([[makeQuery(id+"F8.imprint","IMPRINT",EDGE,{"derivedFrom":subQ3}),1.0]])]});}
            extrude(context, id + "F9", {"entities" : qUnion([Q0, Q1, Q2, Q3]), "operationType" : NewBodyOperationType.ADD, "depth" : 6 * mm, "offsetDistance" : 25 * mm});
        }
    });
